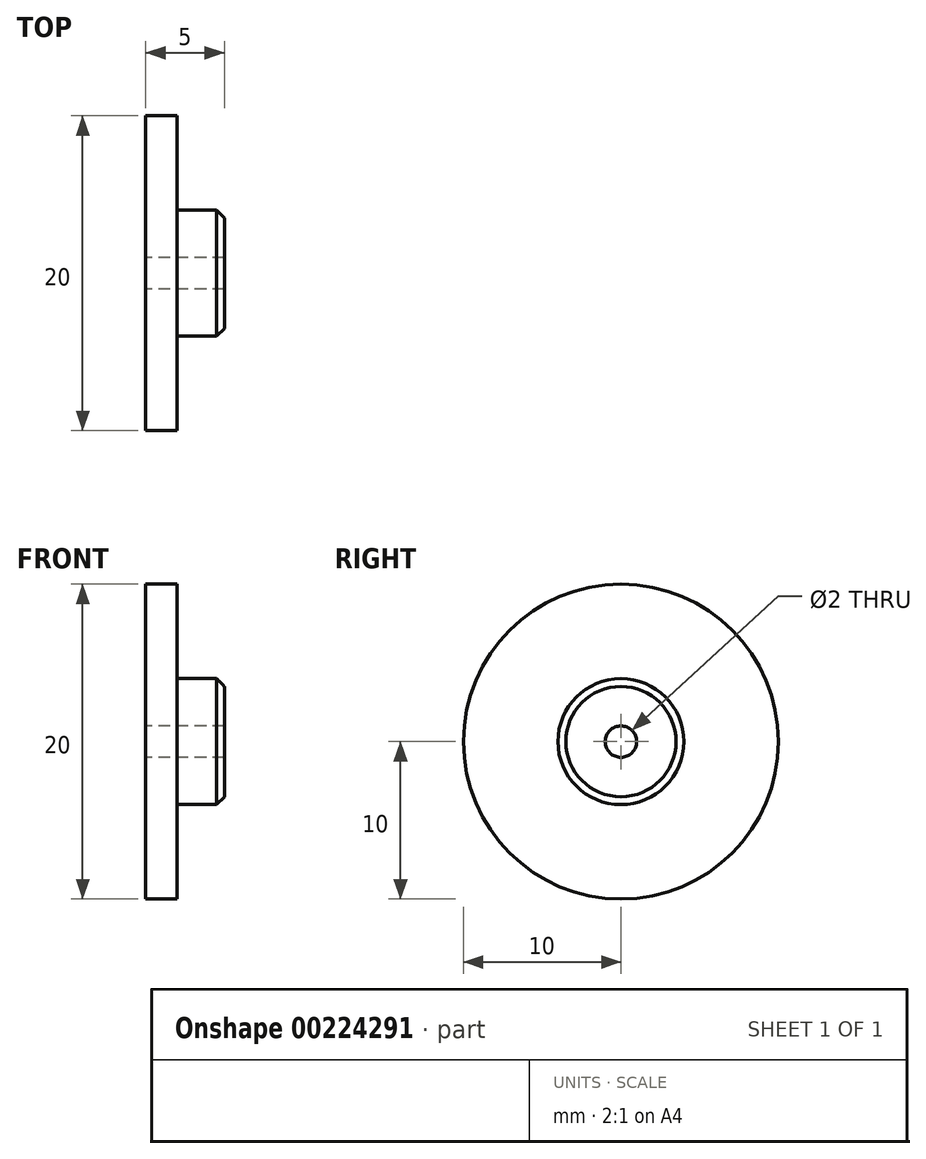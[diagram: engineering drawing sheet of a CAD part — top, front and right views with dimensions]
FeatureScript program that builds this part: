
annotation { "Feature Type Name" : "Feature", "Feature Type Description" : "" }
export const myFeature = defineFeature(function(context is Context, id is Id, definition is map)
    precondition{}
    {
        {
            var Q0;
            Q0=qCreatedBy(makeId("Top.planeOp"),FACE);
            var sketch = newSketch(context, id + "F0", { "sketchPlane" : qUnion([Q0])});
            skLineSegment(sketch, "E0.bottom", {"start": v(0, 1) * mm, "end": v(2, 1) * mm});
            skLineSegment(sketch, "E0.top", {"start": v(0, 10) * mm, "end": v(2, 10) * mm});
            skLineSegment(sketch, "E0.left", {"start": v(0, 1) * mm, "end": v(0, 10) * mm});
            skLineSegment(sketch, "E0.right", {"start": v(2, 1) * mm, "end": v(2, 10) * mm});
            skLineSegment(sketch, "E1.bottom", {"start": v(2, 1) * mm, "end": v(5, 1) * mm});
            skLineSegment(sketch, "E1.top", {"start": v(2, 4) * mm, "end": v(4.5, 4) * mm});
            skLineSegment(sketch, "E1.left", {"start": v(2, 1) * mm, "end": v(2, 4) * mm});
            skLineSegment(sketch, "E1.right", {"start": v(5, 1) * mm, "end": v(5, 3.5) * mm});
            skLineSegment(sketch, "E2", {"start": v(0, 0) * mm, "end": v(10.9, 0) * mm, "construction": true});
            skLineSegment(sketch, "E3", {"start": v(4.5, 4) * mm, "end": v(5, 3.5) * mm});
            skSolve(sketch);
        }
        {
            var Q0;
            Q0=makeQuery(id+"F0.imprint","IMPRINT",FACE,{"disambiguationData":[TD([[makeQuery(id+"F0.imprint","IMPRINT",EDGE,{"derivedFrom":sQuery(id+"F0.wireOp",EDGE,"E0.bottom")}),1.0]])]});
            var Q1;
            Q1=makeQuery(id+"F0.imprint","IMPRINT",FACE,{"disambiguationData":[TD([[makeQuery(id+"F0.imprint","IMPRINT",EDGE,{"derivedFrom":sQuery(id+"F0.wireOp",EDGE,"E1.bottom")}),1.0]])]});
            var Q2;
            Q2=sQuery(id+"F0.wireOp",EDGE,"E2");
            revolve(context, id + "F1", {"entities" : qUnion([Q0, Q1]), "axis" : qUnion([Q2]), "revolveType" : RevolveType.FULL});
        }
    });
